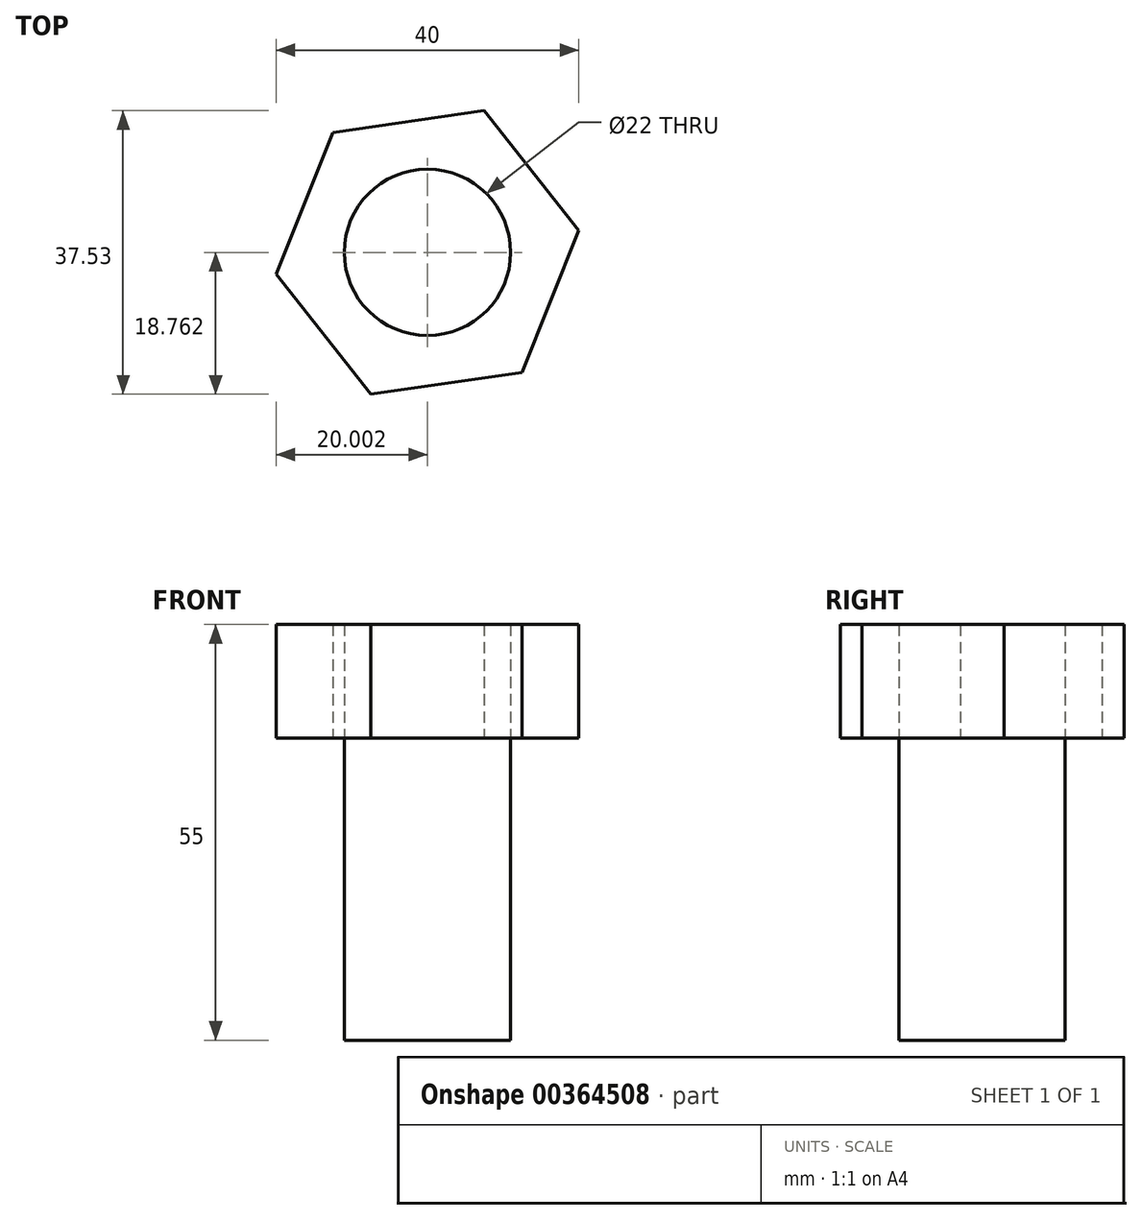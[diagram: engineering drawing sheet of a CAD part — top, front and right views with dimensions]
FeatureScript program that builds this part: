
annotation { "Feature Type Name" : "Feature", "Feature Type Description" : "" }
export const myFeature = defineFeature(function(context is Context, id is Id, definition is map)
    precondition{}
    {
        {
            var Q0;
            Q0=qCreatedBy(makeId("Top.planeOp"),FACE);
            var sketch = newSketch(context, id + "F0", { "sketchPlane" : qUnion([Q0])});
            skCircle(sketch, "E0", {"center": v(-13.75, 22.26) * mm, "radius": 11 * mm});
            skCircle(sketch, "E1.cCircle", {"center": v(-13.75, 22.26) * mm, "radius": 17.5 * mm, "construction": true});
            skLineSegment(sketch, "E1.0", {"start": v(-6.25, 41.03) * mm, "end": v(6.25, 25.15) * mm});
            skLineSegment(sketch, "E1.1", {"start": v(6.25, 25.15) * mm, "end": v(-1.25, 6.39) * mm});
            skLineSegment(sketch, "E1.2", {"start": v(-1.25, 6.39) * mm, "end": v(-21.24, 3.5) * mm});
            skLineSegment(sketch, "E1.3", {"start": v(-21.24, 3.5) * mm, "end": v(-33.75, 19.37) * mm});
            skLineSegment(sketch, "E1.4", {"start": v(-33.75, 19.37) * mm, "end": v(-26.25, 38.14) * mm});
            skLineSegment(sketch, "E1.5", {"start": v(-26.25, 38.14) * mm, "end": v(-6.25, 41.03) * mm});
            skPoint(sketch, "E1.0.midPoint", {"position": v(0, 33.09) * mm});
            skSolve(sketch);
        }
        {
            var Q0;
            Q0=makeQuery(id+"F0.imprint","IMPRINT",FACE,{"disambiguationData":[TD([[makeQuery(id+"F0.imprint","IMPRINT",EDGE,{"derivedFrom":sQuery(id+"F0.wireOp",EDGE,"E0")}),1.0]])]});
            extrude(context, id + "F1", {"entities" : qUnion([Q0]), "oppositeDirection" : true, "depth" : 40 * mm});
        }
        {
            var Q0;
            Q0 = qSketchRegion(id + "F0", true);
            extrude(context, id + "F2", {"entities" : qUnion([Q0]), "depth" : 15 * mm});
        }
        {
            var Q0;
            Q0=makeQuery(id+"F1.opExtrude","CAP_FACE",FACE,{"disambiguationData":[OSD([sQuery(id+"F0.wireOp",EDGE,"E0")])],"isStart":true});
            extrude(context, id + "F3", {"entities" : qUnion([Q0]), "depth" : 15 * mm});
        }
    });
